# Revit family: Cambio Wall Systems - Acoustic - Pin Board 18x36
name_source: partatom
category: Generic Models
units: mm (PartAtom-declared; Revit-internal decimal feet)

## family parameters
Can host rebar = No
Cut with Voids When Loaded = No
Host = Face
Maintain Annotation Orientation = No
Part Type = Normal
Room Calculation Point = No
Round Connector Dimension = Use Diameter
Shared = No

## types (15) — shared parameters
Default Elevation = 4' - 0"

## per-type parameters (varying)
| type | Cambio Material |
| Pin Board Color - BLACK OLIVE | Cambio Pin Board - Black Olive |
| Pin Board Color - BABY LETTUCE | Cambio Pin Board - Baby Lettuce |
| Pin Board Color - BLANCHED ALMOND | Cambio Pin Board - Blanched Almond |
| Pin Board Color - BLUE BERRY | Cambio Pin Board - Blue Berry |
| Pin Board Color - BROWN RICE | Cambio Pin Board - Brown Rice |
| Pin Board Color - CINNAMON BARK | Cambio Pin Board - Cinnamon Bark |
| Pin Board Color - DUCK EGG | Cambio Pin Board - Duck Egg |
| Pin Board Color - FRESH PINEAPPLE | Cambio Pin Board - Fresh Pineapple |
| Pin Board Color - HOT SALSA | Cambio Pin Board - Hot Salsa |
| Pin Board Color - MUSHROOM MEDLEY | Cambio Pin Board - Mushroom Medley |
| Pin Board Color - NUTMEG SPICE | Cambio Pin Board - Nutmeg Spice |
| Pin Board Color - OYSTER SHELL | Cambio Pin Board - Oyster Shell |
| Pin Board Color - POPPY SEED | Cambio Pin Board - Poppy Seed |
| Pin Board Color - POTATO SKIN | Cambio Pin Board - Potato Skin |
| Pin Board Color - TANGERINE ZEST | Cambio Pin Board - Tangerine Zest |

## geometry (parser evidence)
native form markers: Sweep x3
no freeform markers — native parametric forms only
